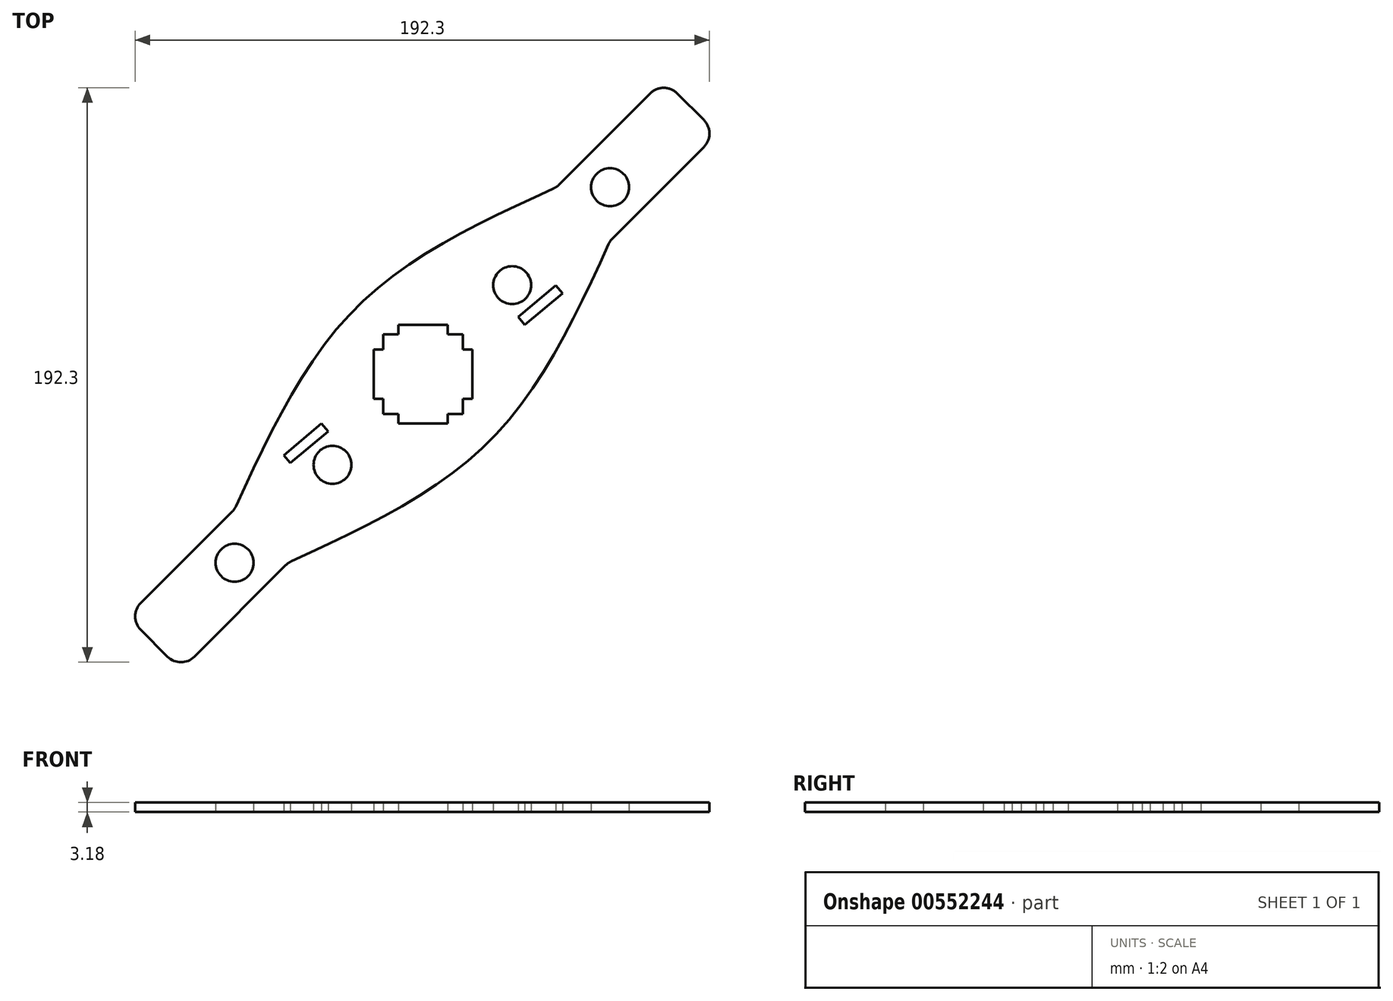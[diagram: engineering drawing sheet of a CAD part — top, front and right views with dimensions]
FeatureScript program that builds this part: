
annotation { "Feature Type Name" : "Feature", "Feature Type Description" : "" }
export const myFeature = defineFeature(function(context is Context, id is Id, definition is map)
    precondition{}
    {
        {
            var Q0;
            Q0=qCreatedBy(makeId("Top.planeOp"),FACE);
            var sketch = newSketch(context, id + "F0", { "sketchPlane" : qUnion([Q0])});
            skLineSegment(sketch, "E0.right", {"start": v(89.53, 89.53) * mm, "end": v(85.04, 94.02) * mm});
            skLineSegment(sketch, "E1.right", {"start": v(-90.07, -90.07) * mm, "end": v(-85.58, -94.56) * mm});
            skCircle(sketch, "E2", {"center": v(-63.13, -63.13) * mm, "radius": 6.35 * mm});
            skCircle(sketch, "E3", {"center": v(-30.35, -30.35) * mm, "radius": 6.35 * mm});
            skCircle(sketch, "E4", {"center": v(62.6, 62.6) * mm, "radius": 6.35 * mm});
            skPoint(sketch, "E5.middle", {"position": v(0, 0) * mm});
            skLineSegment(sketch, "E6", {"start": v(8.26, -13.34) * mm, "end": v(13.34, -13.33) * mm});
            skLineSegment(sketch, "E7", {"start": v(-13.34, -13.34) * mm, "end": v(-8.26, -13.34) * mm});
            skLineSegment(sketch, "E8", {"start": v(-8.26, 13.34) * mm, "end": v(-13.34, 13.34) * mm});
            skLineSegment(sketch, "E9", {"start": v(8.26, 13.34) * mm, "end": v(13.34, 13.34) * mm});
            skLineSegment(sketch, "E10", {"start": v(-76.6, -94.56) * mm, "end": v(-45.97, -63.94) * mm});
            skLineSegment(sketch, "E11", {"start": v(13.34, 8.26) * mm, "end": v(13.34, 13.34) * mm});
            skLineSegment(sketch, "E12", {"start": v(13.34, -8.26) * mm, "end": v(13.34, -13.34) * mm});
            skLineSegment(sketch, "E13", {"start": v(-13.34, 8.26) * mm, "end": v(-13.34, 13.34) * mm});
            skLineSegment(sketch, "E14", {"start": v(-13.33, -8.26) * mm, "end": v(-13.34, -13.34) * mm});
            skLineSegment(sketch, "E15", {"start": v(-94.56, -76.6) * mm, "end": v(-63.94, -45.97) * mm});
            skLineSegment(sketch, "E16", {"start": v(94.02, 76.06) * mm, "end": v(63.4, 45.44) * mm});
            skLineSegment(sketch, "E17", {"start": v(76.06, 94.02) * mm, "end": v(45.44, 63.4) * mm});
            skFitSpline(sketch, "E18", {"points": [v(-45.17, -63.13) * mm, v(22.32, -22.32) * mm, v(62.6, 44.63) * mm], "startDerivative": vector(148.17, 68.22) * mm, "endDerivative": vector(67.3, 147.37) * mm});
            skFitSpline(sketch, "E19", {"points": [v(-63.13, -45.17) * mm, v(-22.32, 22.32) * mm, v(44.63, 62.6) * mm], "startDerivative": vector(68.22, 148.17) * mm, "endDerivative": vector(147.37, 67.3) * mm});
            skCircle(sketch, "E20", {"center": v(29.8, 29.8) * mm, "radius": 6.35 * mm});
            skLineSegment(sketch, "E21", {"start": v(-44.46, -29.74) * mm, "end": v(-31.82, -19.13) * mm});
            skLineSegment(sketch, "E22", {"start": v(31.82, 19.13) * mm, "end": v(44.46, 29.74) * mm});
            skLineSegment(sketch, "E23", {"start": v(-16.51, -8.26) * mm, "end": v(-16.51, 8.26) * mm});
            skLineSegment(sketch, "E24", {"start": v(-16.51, 8.26) * mm, "end": v(-13.34, 8.26) * mm});
            skLineSegment(sketch, "E25", {"start": v(-16.51, -8.26) * mm, "end": v(-13.34, -8.26) * mm});
            skLineSegment(sketch, "E26", {"start": v(-8.26, 16.51) * mm, "end": v(8.26, 16.51) * mm});
            skLineSegment(sketch, "E27", {"start": v(8.26, 16.51) * mm, "end": v(8.26, 13.34) * mm});
            skLineSegment(sketch, "E28", {"start": v(-8.26, 13.34) * mm, "end": v(-8.26, 16.51) * mm});
            skLineSegment(sketch, "E29", {"start": v(16.51, 8.26) * mm, "end": v(16.51, -8.26) * mm});
            skLineSegment(sketch, "E30", {"start": v(16.51, -8.26) * mm, "end": v(13.34, -8.26) * mm});
            skLineSegment(sketch, "E31", {"start": v(16.51, 8.26) * mm, "end": v(13.34, 8.26) * mm});
            skLineSegment(sketch, "E32", {"start": v(8.26, -16.51) * mm, "end": v(-8.26, -16.51) * mm});
            skLineSegment(sketch, "E33", {"start": v(-8.26, -16.51) * mm, "end": v(-8.26, -13.34) * mm});
            skLineSegment(sketch, "E34", {"start": v(8.26, -16.51) * mm, "end": v(8.26, -13.33) * mm});
            skLineSegment(sketch, "E35", {"start": v(34.02, 16.5) * mm, "end": v(46.67, 27.12) * mm});
            skLineSegment(sketch, "E36", {"start": v(44.46, 29.74) * mm, "end": v(31.82, 19.13) * mm});
            skLineSegment(sketch, "E37", {"start": v(31.82, 19.13) * mm, "end": v(34.02, 16.5) * mm});
            skLineSegment(sketch, "E38", {"start": v(44.46, 29.74) * mm, "end": v(46.67, 27.12) * mm});
            skLineSegment(sketch, "E39", {"start": v(-46.67, -27.12) * mm, "end": v(-34.02, -16.5) * mm});
            skLineSegment(sketch, "E40", {"start": v(-31.82, -19.13) * mm, "end": v(-44.46, -29.74) * mm});
            skLineSegment(sketch, "E41", {"start": v(-46.67, -27.12) * mm, "end": v(-44.46, -29.74) * mm});
            skLineSegment(sketch, "E42", {"start": v(-34.02, -16.5) * mm, "end": v(-31.82, -19.13) * mm});
            skArc(sketch, "E43.filletArc", {"start": v(-85.58, -94.56) * mm, "mid": v(-81.1, -96.42) * mm, "end": v(-76.6, -94.56) * mm});
            skArc(sketch, "E44.filletArc", {"start": v(-94.56, -76.6) * mm, "mid": v(-96.42, -81.1) * mm, "end": v(-94.56, -85.58) * mm});
            skArc(sketch, "E45.filletArc", {"start": v(-44.14, -62.66) * mm, "mid": v(-45.11, -63.22) * mm, "end": v(-45.97, -63.94) * mm});
            skArc(sketch, "E46.filletArc", {"start": v(-63.94, -45.97) * mm, "mid": v(-63.22, -45.11) * mm, "end": v(-62.66, -44.14) * mm});
            skArc(sketch, "E47.filletArc", {"start": v(43.59, 62.12) * mm, "mid": v(44.57, 62.68) * mm, "end": v(45.44, 63.4) * mm});
            skArc(sketch, "E48.filletArc", {"start": v(63.4, 45.44) * mm, "mid": v(62.68, 44.57) * mm, "end": v(62.12, 43.59) * mm});
            skArc(sketch, "E49.filletArc", {"start": v(85.04, 94.02) * mm, "mid": v(80.55, 95.88) * mm, "end": v(76.06, 94.02) * mm});
            skArc(sketch, "E50.filletArc", {"start": v(94.02, 76.06) * mm, "mid": v(95.88, 80.55) * mm, "end": v(94.02, 85.04) * mm});
            skLineSegment(sketch, "E51", {"start": v(94.02, 85.04) * mm, "end": v(89.53, 89.53) * mm});
            skLineSegment(sketch, "E52", {"start": v(-90.07, -90.07) * mm, "end": v(-94.56, -85.58) * mm});
            skSolve(sketch);
        }
        {
            var Q0;
            Q0 = qSketchRegion(id + "F0", true);
            extrude(context, id + "F1", {"entities" : qUnion([Q0]), "depth" : 3.17 * mm, "offsetDistance" : 25.4 * mm});
        }
    });
